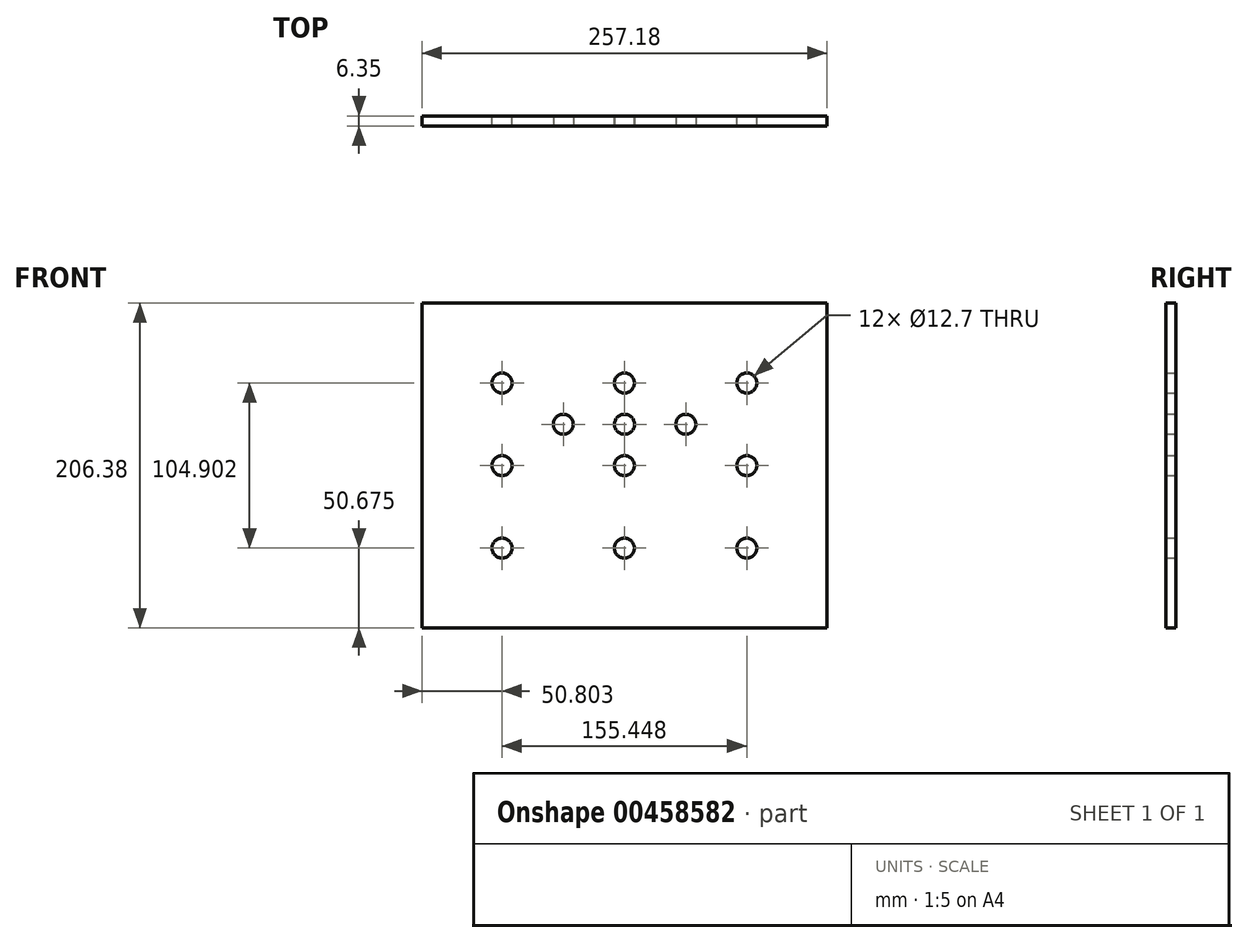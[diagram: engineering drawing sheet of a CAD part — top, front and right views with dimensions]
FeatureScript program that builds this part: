
annotation { "Feature Type Name" : "Feature", "Feature Type Description" : "" }
export const myFeature = defineFeature(function(context is Context, id is Id, definition is map)
    precondition{}
    {
        {
            var Q0;
            Q0=qCreatedBy(makeId("Front.planeOp"),FACE);
            var sketch = newSketch(context, id + "F0", { "sketchPlane" : qUnion([Q0])});
            skLineSegment(sketch, "E0.bottom", {"start": v(103.19, -77.79) * mm, "end": v(-103.19, -77.79) * mm});
            skLineSegment(sketch, "E0.top", {"start": v(103.19, 77.79) * mm, "end": v(-103.19, 77.79) * mm});
            skLineSegment(sketch, "E0.left", {"start": v(103.19, -77.79) * mm, "end": v(103.19, 77.79) * mm});
            skLineSegment(sketch, "E0.right", {"start": v(-103.19, -77.79) * mm, "end": v(-103.19, 77.79) * mm});
            skPoint(sketch, "E0.middle", {"position": v(0, 0) * mm});
            skLineSegment(sketch, "E1.0", {"start": v(128.59, 103.19) * mm, "end": v(-128.59, 103.19) * mm});
            skLineSegment(sketch, "E1.1", {"start": v(128.59, -103.19) * mm, "end": v(128.59, 103.19) * mm});
            skLineSegment(sketch, "E1.2", {"start": v(128.59, -103.19) * mm, "end": v(-128.59, -103.19) * mm});
            skLineSegment(sketch, "E1.3", {"start": v(-128.59, -103.19) * mm, "end": v(-128.59, 103.19) * mm});
            skCircle(sketch, "E2", {"center": v(-77.79, 52.39) * mm, "radius": 6.35 * mm});
            skCircle(sketch, "E3.0.1.0", {"center": v(-77.79, -0.06) * mm, "radius": 6.35 * mm});
            skCircle(sketch, "E3.0.2.0", {"center": v(-77.79, -52.51) * mm, "radius": 6.35 * mm});
            skCircle(sketch, "E3.1.0.0", {"center": v(-0.06, 52.39) * mm, "radius": 6.35 * mm});
            skCircle(sketch, "E3.1.1.0", {"center": v(-0.06, -0.06) * mm, "radius": 6.35 * mm});
            skCircle(sketch, "E3.1.2.0", {"center": v(-0.06, -52.51) * mm, "radius": 6.35 * mm});
            skCircle(sketch, "E3.2.0.0", {"center": v(77.66, 52.39) * mm, "radius": 6.35 * mm});
            skCircle(sketch, "E3.2.1.0", {"center": v(77.66, -0.06) * mm, "radius": 6.35 * mm});
            skCircle(sketch, "E3.2.2.0", {"center": v(77.66, -52.51) * mm, "radius": 6.35 * mm});
            skLineSegment(sketch, "E3.direction1", {"start": v(-77.79, 52.39) * mm, "end": v(-0.06, 52.39) * mm, "construction": true});
            skLineSegment(sketch, "E3.direction2", {"start": v(-77.79, 52.39) * mm, "end": v(-77.79, -0.06) * mm, "construction": true});
            skSolve(sketch);
        }
        {
            var Q0;
            Q0 = qSketchRegion(id + "F0", true);
            var Q1;
            Q1=makeQuery(id+"F0.imprint","IMPRINT",FACE,{"disambiguationData":[TD([[makeQuery(id+"F0.imprint","IMPRINT",EDGE,{"derivedFrom":sQuery(id+"F0.wireOp",EDGE,"E0.bottom")}),-1.0]])]});
            extrude(context, id + "F1", {"entities" : qUnion([Q0, Q1]), "depth" : 6.35 * mm});
        }
        {
            var Q0;
            Q0=makeQuery(id+"F1.opExtrude","CAP_FACE",FACE,{"disambiguationData":[OSD([sQuery(id+"F0.wireOp",EDGE,"E1.0"),sQuery(id+"F0.wireOp",EDGE,"E1.1"),sQuery(id+"F0.wireOp",EDGE,"E1.2"),sQuery(id+"F0.wireOp",EDGE,"E1.3"),sQuery(id+"F0.wireOp",EDGE,"E2"),sQuery(id+"F0.wireOp",EDGE,"E3.0.1.0"),sQuery(id+"F0.wireOp",EDGE,"E3.0.2.0"),sQuery(id+"F0.wireOp",EDGE,"E3.1.0.0"),sQuery(id+"F0.wireOp",EDGE,"E3.1.1.0"),sQuery(id+"F0.wireOp",EDGE,"E3.1.2.0"),sQuery(id+"F0.wireOp",EDGE,"E3.2.0.0"),sQuery(id+"F0.wireOp",EDGE,"E3.2.1.0"),sQuery(id+"F0.wireOp",EDGE,"E3.2.2.0")])],"isStart":false});
            var sketch = newSketch(context, id + "F2", { "sketchPlane" : qUnion([Q0])});
            skCircle(sketch, "E4", {"center": v(-38.9, 26.16) * mm, "radius": 6.35 * mm});
            skCircle(sketch, "E5.1.0.0", {"center": v(0.01, 26.16) * mm, "radius": 6.35 * mm});
            skCircle(sketch, "E5.2.0.0", {"center": v(38.93, 26.16) * mm, "radius": 6.35 * mm});
            skLineSegment(sketch, "E5.direction1", {"start": v(-38.9, 26.16) * mm, "end": v(0.01, 26.16) * mm, "construction": true});
            skPoint(sketch, "E6", {"position": v(-77.79, 52.39) * mm});
            skSolve(sketch);
        }
        {
            var Q0;
            Q0 = qSketchRegion(id + "F2", true);
            extrude(context, id + "F3", {"entities" : qUnion([Q0]), "operationType" : NewBodyOperationType.REMOVE, "oppositeDirection" : true, "depth" : 25.4 * mm});
        }
    });
